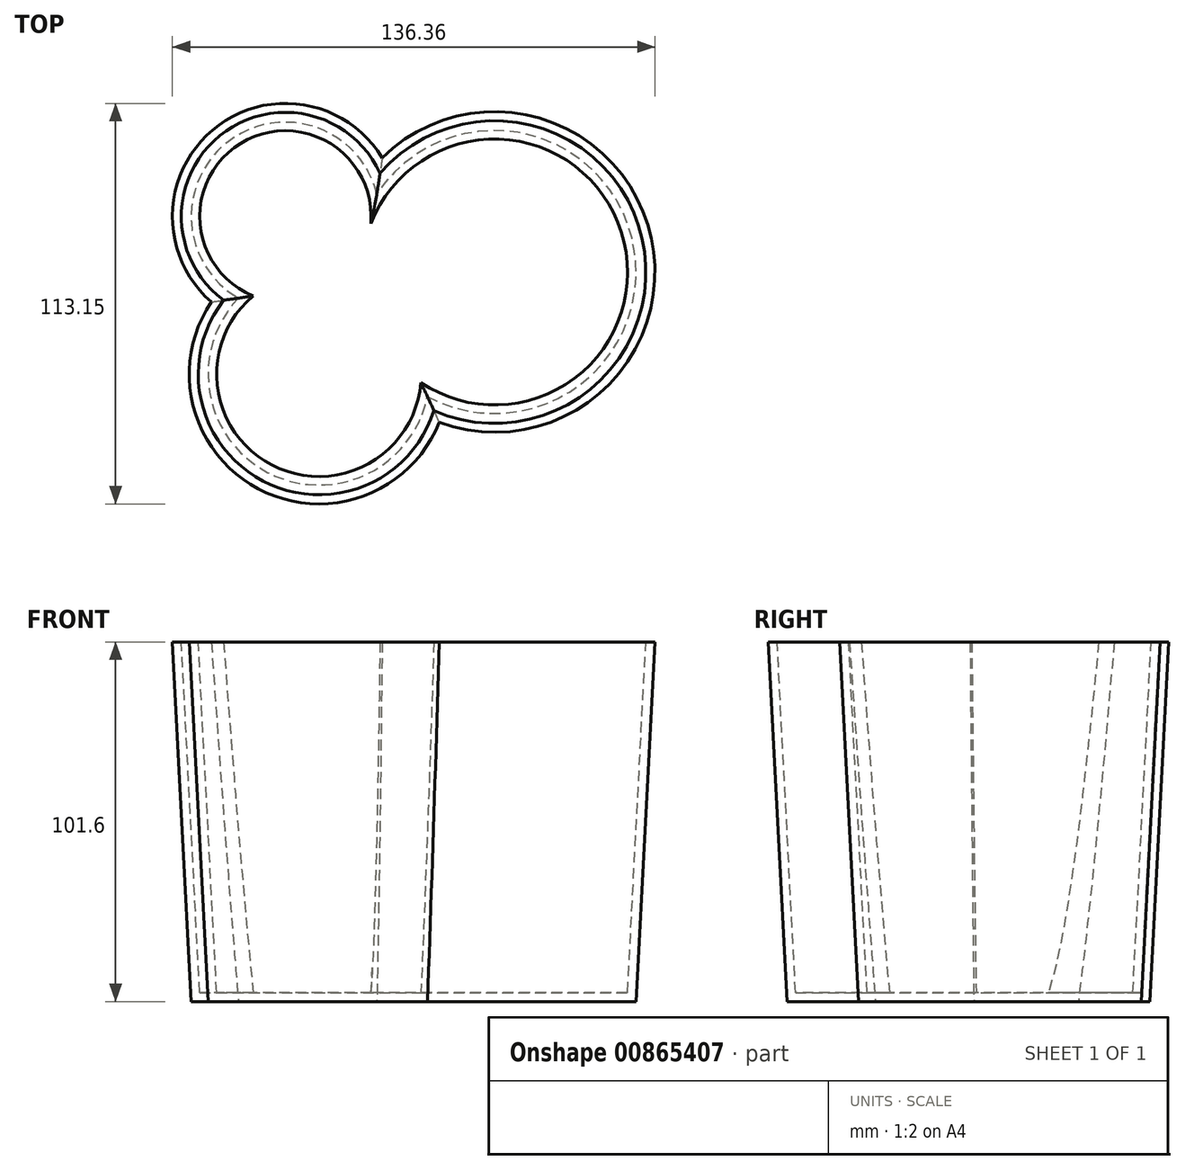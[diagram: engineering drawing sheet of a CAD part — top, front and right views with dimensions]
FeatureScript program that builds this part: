
annotation { "Feature Type Name" : "Feature", "Feature Type Description" : "" }
export const myFeature = defineFeature(function(context is Context, id is Id, definition is map)
    precondition{}
    {
        {
            var Q0;
            Q0=qCreatedBy(makeId("Top.planeOp"),FACE);
            var sketch = newSketch(context, id + "F0", { "sketchPlane" : qUnion([Q0])});
            skArc(sketch, "E0", {"start": v(-15.38, 28.83) * mm, "mid": v(-57.25, 43.66) * mm, "end": v(-54.51, -0.67) * mm});
            skArc(sketch, "E1", {"start": v(-1.08, -28.48) * mm, "mid": v(56.67, 16.37) * mm, "end": v(-15.38, 28.83) * mm});
            skArc(sketch, "E2", {"start": v(-54.51, -0.67) * mm, "mid": v(-46.2, -49.94) * mm, "end": v(-1.08, -28.48) * mm});
            skSolve(sketch);
        }
        {
            var Q0;
            Q0=makeQuery(id+"F0.imprint","IMPRINT",FACE,{"disambiguationData":[TD([[makeQuery(id+"F0.imprint","IMPRINT",EDGE,{"derivedFrom":sQuery(id+"F0.wireOp",EDGE,"E0")}),1.0]])]});
            extrude(context, id + "F1", {"entities" : qUnion([Q0]), "depth" : 101.6 * mm, "offsetDistance" : 25.4 * mm, "hasDraft" : true, "draftAngle" : 3 * degree});
        }
        {
            var Q0;
            Q0=makeQuery(id+"F1.opExtrude","CAP_FACE",FACE,{"disambiguationData":[OSD([sQuery(id+"F0.wireOp",EDGE,"E0"),sQuery(id+"F0.wireOp",EDGE,"E1"),sQuery(id+"F0.wireOp",EDGE,"E2")])],"isStart":false});
            shell(context, id + "F2", {"entities" : qUnion([Q0]), "thickness" : 2.54 * mm});
        }
    });
